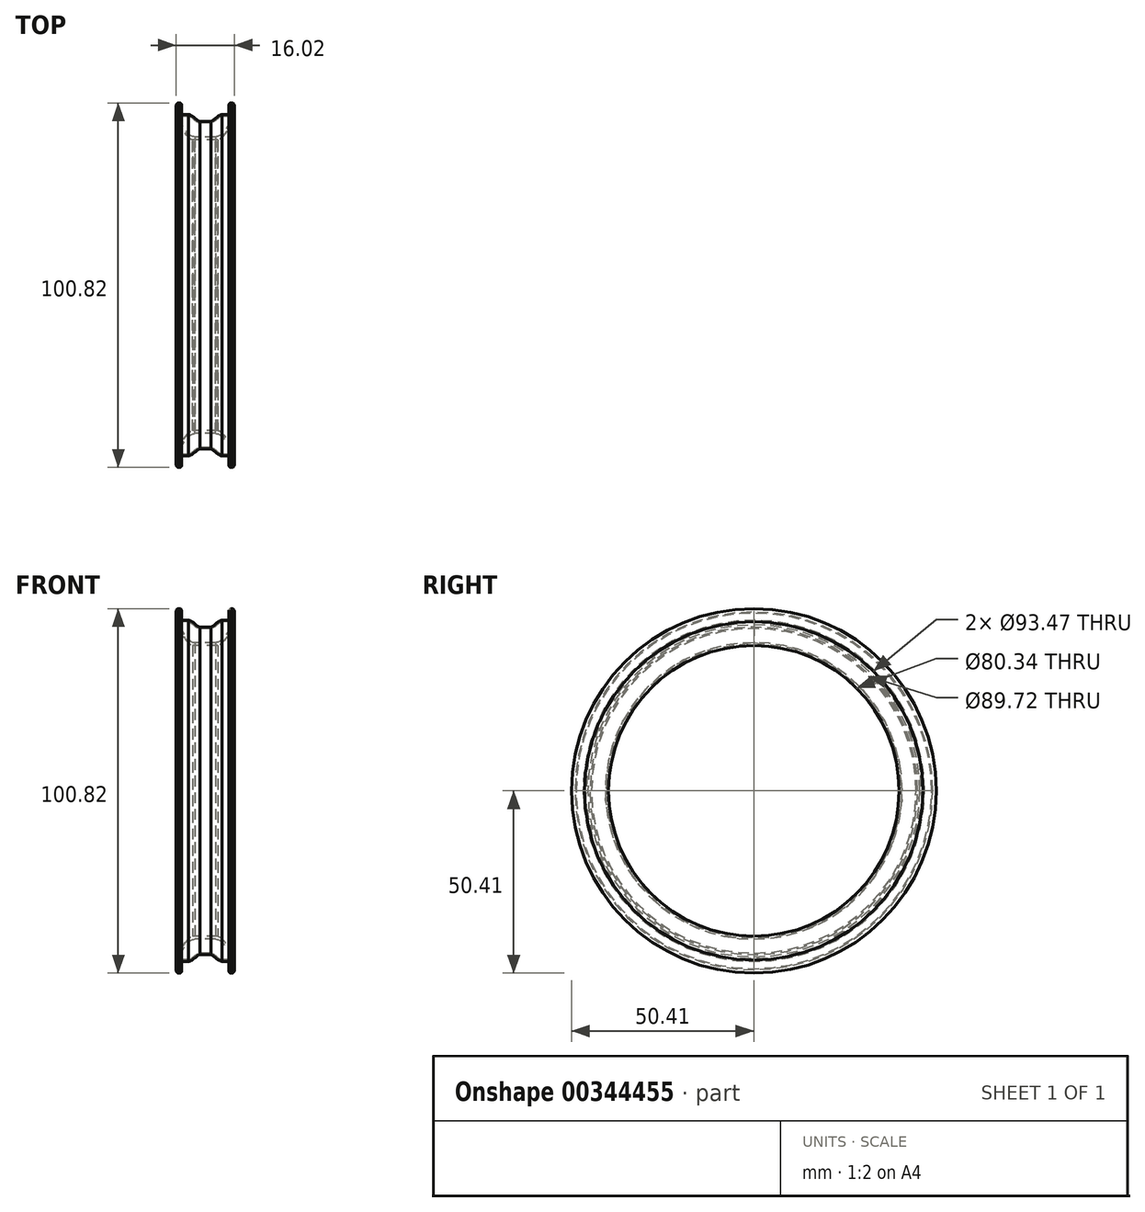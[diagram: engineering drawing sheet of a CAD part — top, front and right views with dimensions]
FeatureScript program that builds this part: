
annotation { "Feature Type Name" : "Feature", "Feature Type Description" : "" }
export const myFeature = defineFeature(function(context is Context, id is Id, definition is map)
    precondition{}
    {
        {
            var Q0;
            Q0=qCreatedBy(makeId("Front.planeOp"),FACE);
            var sketch = newSketch(context, id + "F0", { "sketchPlane" : qUnion([Q0])});
            skFitSpline(sketch, "E0", {"points": [v(-8.01, 46.77) * mm, v(-3.46, 40.17) * mm], "startDerivative": vector(1.27, -6) * mm, "endDerivative": vector(4.03, -0.47) * mm});
            skLineSegment(sketch, "E1", {"start": v(-3.46, 40.17) * mm, "end": v(0, 40.17) * mm});
            skLineSegment(sketch, "E2", {"start": v(-8.01, 46.77) * mm, "end": v(-8.01, 49.72) * mm});
            skLineSegment(sketch, "E3", {"start": v(-1.52, 44.86) * mm, "end": v(0, 44.86) * mm});
            skArc(sketch, "E4", {"start": v(-8.01, 49.72) * mm, "mid": v(-7.84, 50.18) * mm, "end": v(-7.42, 50.41) * mm});
            skLineSegment(sketch, "E5", {"start": v(-7.42, 50.41) * mm, "end": v(-7.07, 50.41) * mm});
            skArc(sketch, "E6", {"start": v(-7.07, 50.41) * mm, "mid": v(-6.59, 49.93) * mm, "end": v(-7.07, 49.44) * mm});
            skArc(sketch, "E7", {"start": v(-7.07, 49.44) * mm, "mid": v(-7.26, 49.36) * mm, "end": v(-7.32, 49.16) * mm});
            skLineSegment(sketch, "E8", {"start": v(-7.32, 49.16) * mm, "end": v(-7.32, 47.72) * mm});
            skArc(sketch, "E9", {"start": v(-7.32, 47.72) * mm, "mid": v(-7.16, 47.32) * mm, "end": v(-6.76, 47.16) * mm});
            skLineSegment(sketch, "E10", {"start": v(-6.76, 47.16) * mm, "end": v(-4.62, 47.16) * mm});
            skFitSpline(sketch, "E11", {"points": [v(-4.62, 47.16) * mm, v(-1.52, 45.3) * mm], "startDerivative": vector(3.14, 0) * mm, "endDerivative": vector(2.06, 0) * mm});
            skFitSpline(sketch, "E12", {"points": [v(-4.6, 46.74) * mm, v(-1.52, 44.86) * mm], "startDerivative": vector(1.88, 0.28) * mm, "endDerivative": vector(3, -0.23) * mm});
            skLineSegment(sketch, "E13", {"start": v(-1.52, 45.3) * mm, "end": v(0, 45.3) * mm});
            skLineSegment(sketch, "E14", {"start": v(-4.6, 46.74) * mm, "end": v(-6.59, 46.74) * mm});
            skArc(sketch, "E15", {"start": v(-6.59, 46.74) * mm, "mid": v(-7.13, 46.47) * mm, "end": v(-7.25, 45.88) * mm});
            skFitSpline(sketch, "E16", {"points": [v(-7.25, 45.88) * mm, v(-2.88, 41.01) * mm], "startDerivative": vector(0.6, -1.22) * mm, "endDerivative": vector(6.7, 0.19) * mm});
            skLineSegment(sketch, "E17", {"start": v(-2.88, 41.01) * mm, "end": v(0, 41.01) * mm});
            skLineSegment(sketch, "E18.MirrorCS", {"start": v(7.42, 50.41) * mm, "end": v(7.07, 50.41) * mm});
            skArc(sketch, "E19.MirrorCS", {"start": v(7.07, 49.44) * mm, "mid": v(7.26, 49.36) * mm, "end": v(7.32, 49.16) * mm});
            skArc(sketch, "E20.MirrorCS", {"start": v(6.59, 46.74) * mm, "mid": v(7.13, 46.47) * mm, "end": v(7.25, 45.88) * mm});
            skArc(sketch, "E21.MirrorCS", {"start": v(7.32, 47.72) * mm, "mid": v(7.16, 47.32) * mm, "end": v(6.76, 47.16) * mm});
            skLineSegment(sketch, "E22.MirrorCS", {"start": v(2.88, 41.01) * mm, "end": v(0, 41.01) * mm});
            skLineSegment(sketch, "E23.MirrorCS", {"start": v(6.76, 47.16) * mm, "end": v(4.62, 47.16) * mm});
            skFitSpline(sketch, "E24.MirrorCS", {"points": [v(4.62, 47.16) * mm, v(1.52, 45.3) * mm], "startDerivative": vector(-3.14, 0) * mm, "endDerivative": vector(-2.06, 0) * mm});
            skLineSegment(sketch, "E25.MirrorCS", {"start": v(1.52, 45.3) * mm, "end": v(0, 45.3) * mm});
            skLineSegment(sketch, "E26.MirrorCS", {"start": v(8.01, 46.77) * mm, "end": v(8.01, 49.72) * mm});
            skLineSegment(sketch, "E27.MirrorCS", {"start": v(4.6, 46.74) * mm, "end": v(6.59, 46.74) * mm});
            skLineSegment(sketch, "E28.MirrorCS", {"start": v(3.46, 40.17) * mm, "end": v(0, 40.17) * mm});
            skArc(sketch, "E29.MirrorCS", {"start": v(7.07, 50.41) * mm, "mid": v(6.59, 49.93) * mm, "end": v(7.07, 49.44) * mm});
            skLineSegment(sketch, "E30.MirrorCS", {"start": v(1.52, 44.86) * mm, "end": v(0, 44.86) * mm});
            skArc(sketch, "E31.MirrorCS", {"start": v(8.01, 49.72) * mm, "mid": v(7.84, 50.18) * mm, "end": v(7.42, 50.41) * mm});
            skFitSpline(sketch, "E32.MirrorCS", {"points": [v(8.01, 46.77) * mm, v(3.46, 40.17) * mm], "startDerivative": vector(-1.27, -6) * mm, "endDerivative": vector(-4.03, -0.47) * mm});
            skLineSegment(sketch, "E33.MirrorCS", {"start": v(7.32, 49.16) * mm, "end": v(7.32, 47.72) * mm});
            skFitSpline(sketch, "E34.MirrorCS", {"points": [v(4.6, 46.74) * mm, v(1.52, 44.86) * mm], "startDerivative": vector(-1.88, 0.28) * mm, "endDerivative": vector(-3, -0.23) * mm});
            skFitSpline(sketch, "E35.MirrorCS", {"points": [v(7.25, 45.88) * mm, v(2.88, 41.01) * mm], "startDerivative": vector(-0.6, -1.22) * mm, "endDerivative": vector(-6.7, 0.19) * mm});
            skLineSegment(sketch, "E36", {"start": v(-14.29, 0) * mm, "end": v(15.1, 0) * mm, "construction": true});
            skLineSegment(sketch, "E37", {"start": v(-8.01, 51.67) * mm, "end": v(0, 51.67) * mm, "construction": true});
            skSolve(sketch);
        }
        {
            var Q0;
            Q0=makeQuery(id+"F0.imprint","IMPRINT",FACE,{"disambiguationData":[TD([[makeQuery(id+"F0.imprint","IMPRINT",EDGE,{"derivedFrom":sQuery(id+"F0.wireOp",EDGE,"E0")}),1.0]])]});
            var Q1;
            Q1=sQuery(id+"F0.wireOp",EDGE,"E36");
            revolve(context, id + "F1", {"entities" : qUnion([Q0]), "axis" : qUnion([Q1]), "revolveType" : RevolveType.FULL});
        }
    });
